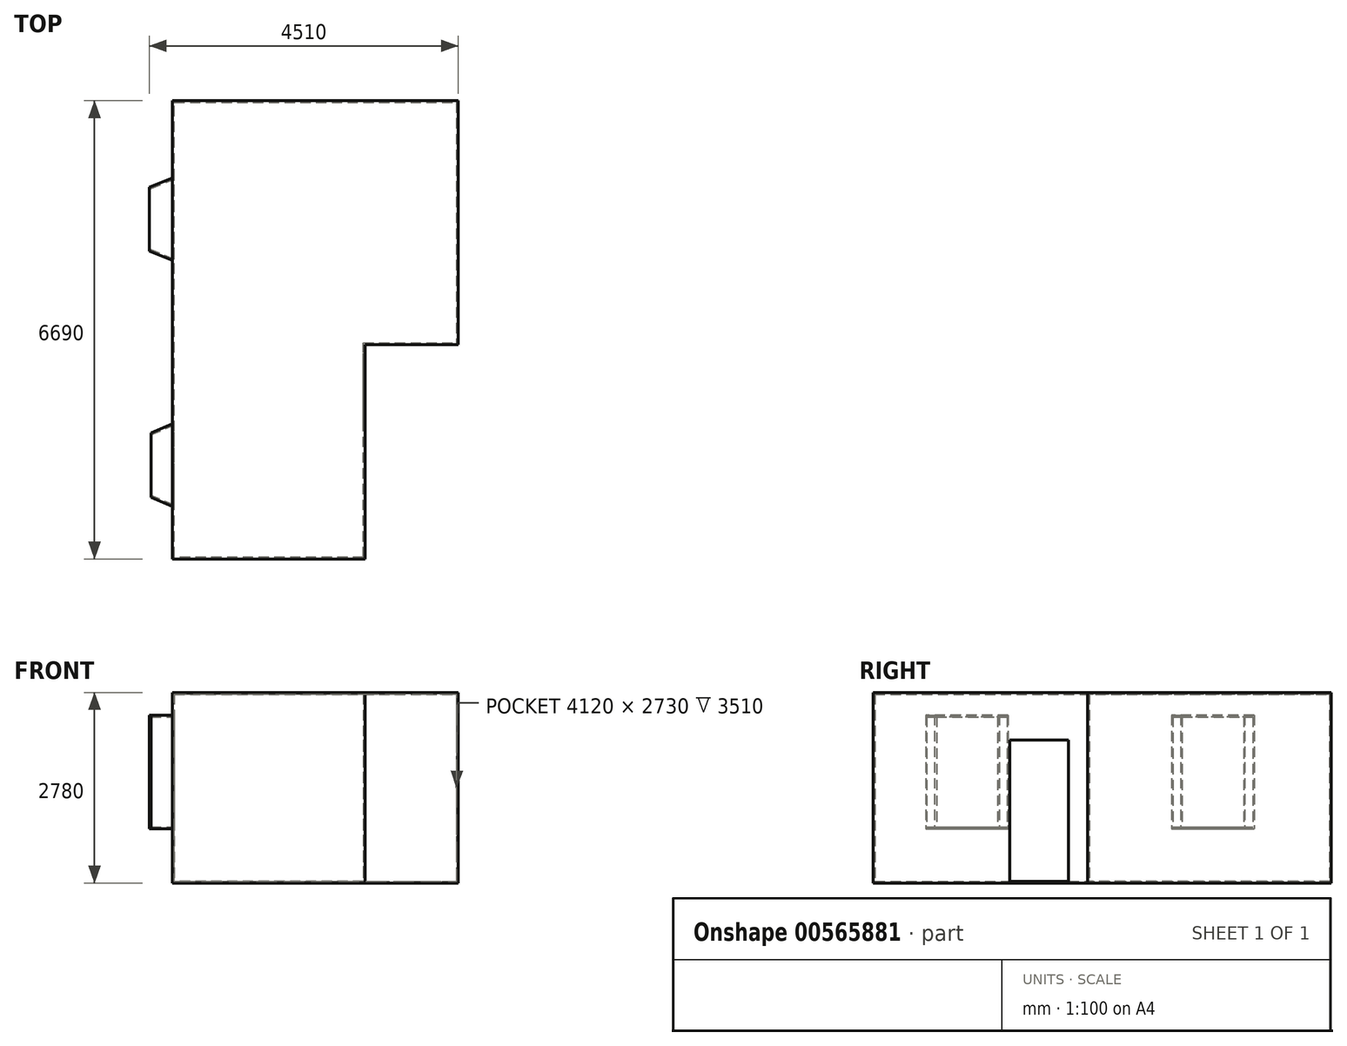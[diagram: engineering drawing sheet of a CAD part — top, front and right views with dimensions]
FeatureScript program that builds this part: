
annotation { "Feature Type Name" : "Feature", "Feature Type Description" : "" }
export const myFeature = defineFeature(function(context is Context, id is Id, definition is map)
    precondition{}
    {
        {
            var Q0;
            Q0=qCreatedBy(makeId("Top.planeOp"),FACE);
            var sketch = newSketch(context, id + "F0", { "sketchPlane" : qUnion([Q0])});
            skLineSegment(sketch, "E0.bottom", {"start": v(0, 0) * mm, "end": v(-2760, 0) * mm});
            skLineSegment(sketch, "E0.left", {"start": v(0, 0) * mm, "end": v(0, 3130) * mm});
            skLineSegment(sketch, "E0.right", {"start": v(-2760, 0) * mm, "end": v(-2760, 760) * mm});
            skLineSegment(sketch, "E1.top", {"start": v(0, 3130) * mm, "end": v(1360, 3130) * mm});
            skLineSegment(sketch, "E1.right", {"start": v(1360, 6640) * mm, "end": v(1360, 3130) * mm});
            skLineSegment(sketch, "E2", {"start": v(-2760, 6640) * mm, "end": v(1360, 6640) * mm});
            skLineSegment(sketch, "E3", {"start": v(-2760, 760) * mm, "end": v(-3100, 900) * mm});
            skLineSegment(sketch, "E4", {"start": v(-3100, 900) * mm, "end": v(-3100, 1790) * mm});
            skLineSegment(sketch, "E5", {"start": v(-3100, 1790) * mm, "end": v(-2760, 1930) * mm});
            skLineSegment(sketch, "E6.trimOffspring", {"start": v(-2760, 1930) * mm, "end": v(-2760, 4350) * mm});
            skLineSegment(sketch, "E7", {"start": v(-2760, 4350) * mm, "end": v(-3100, 4485) * mm});
            skLineSegment(sketch, "E8", {"start": v(-3100, 4485) * mm, "end": v(-3100, 5385) * mm});
            skLineSegment(sketch, "E9", {"start": v(-3100, 5385) * mm, "end": v(-2760, 5520) * mm});
            skLineSegment(sketch, "E10.trimOffspring", {"start": v(-2760, 5520) * mm, "end": v(-2760, 6640) * mm});
            skSolve(sketch);
        }
        {
            var Q0;
            Q0 = qSketchRegion(id + "F0", true);
            extrude(context, id + "F1", {"entities" : qUnion([Q0]), "depth" : 2730 * mm, "offsetDistance" : 25 * mm});
        }
        {
            var Q0;
            Q0=makeQuery(id+"F1.opExtrude","CAP_FACE",FACE,{"disambiguationData":[OSD([sQuery(id+"F0.wireOp",EDGE,"E0.bottom"),sQuery(id+"F0.wireOp",EDGE,"E0.left"),sQuery(id+"F0.wireOp",EDGE,"E0.right"),sQuery(id+"F0.wireOp",EDGE,"E1.top"),sQuery(id+"F0.wireOp",EDGE,"E1.right"),sQuery(id+"F0.wireOp",EDGE,"E2"),sQuery(id+"F0.wireOp",EDGE,"E3"),sQuery(id+"F0.wireOp",EDGE,"E4"),sQuery(id+"F0.wireOp",EDGE,"E5"),sQuery(id+"F0.wireOp",EDGE,"E6.trimOffspring"),sQuery(id+"F0.wireOp",EDGE,"E7"),sQuery(id+"F0.wireOp",EDGE,"E8"),sQuery(id+"F0.wireOp",EDGE,"E9"),sQuery(id+"F0.wireOp",EDGE,"E10.trimOffspring")])],"isStart":true});
            var sketch = newSketch(context, id + "F2", { "sketchPlane" : qUnion([Q0])});
            skLineSegment(sketch, "E11", {"start": v(-2760, -5520) * mm, "end": v(-3100, -5385) * mm});
            skLineSegment(sketch, "E12", {"start": v(-3100, -5385) * mm, "end": v(-3100, -4485) * mm});
            skLineSegment(sketch, "E13", {"start": v(-3100, -4485) * mm, "end": v(-2760, -4350) * mm});
            skLineSegment(sketch, "E14", {"start": v(-2760, -4350) * mm, "end": v(-2760, -5520) * mm});
            skSolve(sketch);
        }
        {
            var Q0;
            Q0 = qSketchRegion(id + "F2", true);
            extrude(context, id + "F3", {"entities" : qUnion([Q0]), "operationType" : NewBodyOperationType.REMOVE, "oppositeDirection" : true, "depth" : 790 * mm, "offsetDistance" : 25 * mm});
        }
        {
            var Q0;
            Q0=makeQuery(id+"F1.opExtrude","CAP_FACE",FACE,{"disambiguationData":[OSD([sQuery(id+"F0.wireOp",EDGE,"E0.bottom"),sQuery(id+"F0.wireOp",EDGE,"E0.left"),sQuery(id+"F0.wireOp",EDGE,"E0.right"),sQuery(id+"F0.wireOp",EDGE,"E1.top"),sQuery(id+"F0.wireOp",EDGE,"E1.right"),sQuery(id+"F0.wireOp",EDGE,"E2"),sQuery(id+"F0.wireOp",EDGE,"E3"),sQuery(id+"F0.wireOp",EDGE,"E4"),sQuery(id+"F0.wireOp",EDGE,"E5"),sQuery(id+"F0.wireOp",EDGE,"E6.trimOffspring"),sQuery(id+"F0.wireOp",EDGE,"E7"),sQuery(id+"F0.wireOp",EDGE,"E8"),sQuery(id+"F0.wireOp",EDGE,"E9"),sQuery(id+"F0.wireOp",EDGE,"E10.trimOffspring")])],"isStart":true});
            var sketch = newSketch(context, id + "F4", { "sketchPlane" : qUnion([Q0])});
            skLineSegment(sketch, "E15", {"start": v(-2760, -1930) * mm, "end": v(-3100, -1790) * mm});
            skLineSegment(sketch, "E16", {"start": v(-3100, -1790) * mm, "end": v(-3100, -900) * mm});
            skLineSegment(sketch, "E17", {"start": v(-3100, -900) * mm, "end": v(-2760, -760) * mm});
            skLineSegment(sketch, "E18", {"start": v(-2760, -760) * mm, "end": v(-2760, -1930) * mm});
            skSolve(sketch);
        }
        {
            var Q0;
            Q0 = qSketchRegion(id + "F4", true);
            extrude(context, id + "F5", {"entities" : qUnion([Q0]), "operationType" : NewBodyOperationType.REMOVE, "oppositeDirection" : true, "depth" : 790 * mm, "offsetDistance" : 25 * mm});
        }
        {
            var Q0;
            Q0=makeQuery(id+"F1.opExtrude","CAP_FACE",FACE,{"disambiguationData":[OSD([sQuery(id+"F0.wireOp",EDGE,"E0.bottom"),sQuery(id+"F0.wireOp",EDGE,"E0.left"),sQuery(id+"F0.wireOp",EDGE,"E0.right"),sQuery(id+"F0.wireOp",EDGE,"E1.top"),sQuery(id+"F0.wireOp",EDGE,"E1.right"),sQuery(id+"F0.wireOp",EDGE,"E2"),sQuery(id+"F0.wireOp",EDGE,"E3"),sQuery(id+"F0.wireOp",EDGE,"E4"),sQuery(id+"F0.wireOp",EDGE,"E5"),sQuery(id+"F0.wireOp",EDGE,"E6.trimOffspring"),sQuery(id+"F0.wireOp",EDGE,"E7"),sQuery(id+"F0.wireOp",EDGE,"E8"),sQuery(id+"F0.wireOp",EDGE,"E9"),sQuery(id+"F0.wireOp",EDGE,"E10.trimOffspring")])],"isStart":true});
            cPlane(context, id + "F6", {"entities" : qUnion([Q0]), "cplaneType" : CPlaneType.OFFSET, "offset" : 2400 * mm, "oppositeDirection" : true, "width" : 150 * mm, "height" : 150 * mm});
        }
        {
            var Q0;
            Q0=qCreatedBy(id+"F6.planeOp",FACE);
            var sketch = newSketch(context, id + "F7", { "sketchPlane" : qUnion([Q0])});
            skLineSegment(sketch, "E19.0.0", {"start": v(-2760, -1930) * mm, "end": v(-2760, -760) * mm});
            skLineSegment(sketch, "E19.0.1", {"start": v(-2760, -760) * mm, "end": v(-3100, -900) * mm});
            skLineSegment(sketch, "E19.0.2", {"start": v(-3100, -900) * mm, "end": v(-3100, -1790) * mm});
            skLineSegment(sketch, "E19.0.3", {"start": v(-3100, -1790) * mm, "end": v(-2760, -1930) * mm});
            skSolve(sketch);
        }
        {
            var Q0;
            Q0 = qSketchRegion(id + "F7", true);
            extrude(context, id + "F8", {"entities" : qUnion([Q0]), "operationType" : NewBodyOperationType.REMOVE, "endBound" : BoundingType.UP_TO_NEXT, "oppositeDirection" : true, "depth" : 25 * mm, "offsetDistance" : 25 * mm});
        }
        {
            var Q0;
            Q0=qCreatedBy(id+"F6.planeOp",FACE);
            var sketch = newSketch(context, id + "F9", { "sketchPlane" : qUnion([Q0])});
            skLineSegment(sketch, "E20.0.0", {"start": v(-2760, -5520) * mm, "end": v(-2760, -4350) * mm});
            skLineSegment(sketch, "E20.0.1", {"start": v(-2760, -4350) * mm, "end": v(-3100, -4485) * mm});
            skLineSegment(sketch, "E20.0.2", {"start": v(-3100, -4485) * mm, "end": v(-3100, -5385) * mm});
            skLineSegment(sketch, "E20.0.3", {"start": v(-3100, -5385) * mm, "end": v(-2760, -5520) * mm});
            skSolve(sketch);
        }
        {
            var Q0;
            Q0 = qSketchRegion(id + "F9", true);
            extrude(context, id + "F10", {"entities" : qUnion([Q0]), "operationType" : NewBodyOperationType.REMOVE, "endBound" : BoundingType.UP_TO_NEXT, "oppositeDirection" : true, "depth" : 25 * mm, "offsetDistance" : 25 * mm});
        }
        {
            var Q0;
            Q0=makeQuery(id+"F1.opExtrude","SWEPT_FACE",FACE,{"disambiguationData":[OSD([sQuery(id+"F0.wireOp",EDGE,"E4")])]});
            shell(context, id + "F11", {"entities" : qUnion([Q0]), "thickness" : 25 * mm, "oppositeDirection" : true});
        }
        {
            var Q0;
            Q0=makeQuery(id+"F11.opShell","OFFSET_FACE",FACE,{"disambiguationData":[OSD([sQuery(id+"F0.wireOp",EDGE,"E8")])]});
            var sketch = newSketch(context, id + "F12", { "sketchPlane" : qUnion([Q0])});
            skLineSegment(sketch, "E21.0.0", {"start": v(4485, 2400) * mm, "end": v(4485, 790) * mm});
            skLineSegment(sketch, "E21.0.1", {"start": v(4485, 790) * mm, "end": v(5385, 790) * mm});
            skLineSegment(sketch, "E21.0.2", {"start": v(5385, 790) * mm, "end": v(5385, 2400) * mm});
            skLineSegment(sketch, "E21.0.3", {"start": v(5385, 2400) * mm, "end": v(4485, 2400) * mm});
            skSolve(sketch);
        }
        {
            var Q0;
            Q0 = qSketchRegion(id + "F12", true);
            extrude(context, id + "F13", {"entities" : qUnion([Q0]), "operationType" : NewBodyOperationType.REMOVE, "endBound" : BoundingType.UP_TO_NEXT, "oppositeDirection" : true, "depth" : 25 * mm, "offsetDistance" : 25 * mm});
        }
        {
            var Q0;
            Q0=makeQuery(id+"F1.opExtrude","SWEPT_FACE",FACE,{"disambiguationData":[OSD([sQuery(id+"F0.wireOp",EDGE,"E0.left")])]});
            var sketch = newSketch(context, id + "F14", { "sketchPlane" : qUnion([Q0])});
            skLineSegment(sketch, "E22.bottom", {"start": v(1970, 2060) * mm, "end": v(2830, 2060) * mm});
            skLineSegment(sketch, "E22.top", {"start": v(1970, 0) * mm, "end": v(2830, 0) * mm});
            skLineSegment(sketch, "E22.left", {"start": v(1970, 2060) * mm, "end": v(1970, 0) * mm});
            skLineSegment(sketch, "E22.right", {"start": v(2830, 2060) * mm, "end": v(2830, 0) * mm});
            skLineSegment(sketch, "E23.0.0", {"start": v(3130, 0) * mm, "end": v(0, 0) * mm});
            skLineSegment(sketch, "E23.0.1", {"start": v(0, 0) * mm, "end": v(0, 2730) * mm});
            skLineSegment(sketch, "E23.0.2", {"start": v(0, 2730) * mm, "end": v(3130, 2730) * mm});
            skLineSegment(sketch, "E23.0.3", {"start": v(3130, 2730) * mm, "end": v(3130, 0) * mm});
            skSolve(sketch);
        }
        {
            var Q0;
            Q0=makeQuery(id+"F14.imprint","IMPRINT",FACE,{"disambiguationData":[TD([[makeQuery(id+"F14.imprint","IMPRINT",EDGE,{"derivedFrom":sQuery(id+"F14.wireOp",EDGE,"E22.bottom")}),-1.0]])]});
            extrude(context, id + "F15", {"entities" : qUnion([Q0]), "operationType" : NewBodyOperationType.REMOVE, "endBound" : BoundingType.UP_TO_NEXT, "oppositeDirection" : true, "depth" : 25 * mm, "offsetDistance" : 25 * mm});
        }
    });
